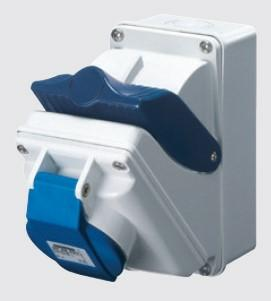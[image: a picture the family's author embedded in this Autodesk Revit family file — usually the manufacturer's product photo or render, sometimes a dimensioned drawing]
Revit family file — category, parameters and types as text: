
# Revit family: Building-ConnessioniIEC309-GEWISS-COMBIBLOC-PRESE-INTERBLOCCATE_IP44
name_source: partatom
category: Apparecchi elettrici
units: mm (PartAtom-declared; Revit-internal decimal feet)

## family parameters
Condiviso = No
Host = Superficie
Mantenere orientamento annotazione = Sì
Punto di calcolo locali = Sì
Quota connettore circolare = Usa diametro
Taglio con vuoti quando caricato = No
Tipo di parte = Normale

## types (18) — shared parameters
BLOCCO = B=C
Catalogo = BUILDING
Codice Electrocod = 2220
Con fondo = Si
FORMULA = 1000 mm  [stored 3.28084 ft]
Frequenza = 50/60 Hz
Glow wire test: = 850 °C (Parti attive) - 650 °C (Parti passive)
Grado di protezione = IP44
IDF = 30b8ffdf-9bd3-4092-bfeb-7357e213d0d1
IDT = 5f0ae1981d6d44abab9cf411e87918d1
Immagine tipo = COMBIBLOC44Fondo.jpg
L = 155 mm
N.poli = 1
POMELLO = bianco
PRESA = Giallo
Produttore = GEWISS S.p.A.
Prospetto di default = 1219 mm
Protezione = NO (SBF)
Resistenza agli urti = IK08
SEO = Presa interbloccata
STRUTTURA = RAL - 7035
STRUTTURA ALTA = blue
Scheda Tecnica = https://www.gewiss.com
Spostamento_S = 1500 mm
Temperatura di utilizzo = -25 +40 °C
Termopressione con biglia = 125 °C (Parti attive) - 80 °C (Parti passive)
Tipologia = Compatta
URL = https://www.gewiss.com
VETRO = Vetro
Versione file RFA = 21.4
Voltaggio = 0 V
W = 115 mm

## per-type parameters (varying)
| type | Colore: | Corrente nominale (A) | Descrizione | Modello | N. poli | Riferimento h | Tensione nominale |
| GW66405 - COMBIBLOC C.F.IP44 3P+T 16A 230V 9H | Blu | 16 | COMBIBLOC C.F.IP44 3P+T 16A 230V 9H | GW66405 | 3P+T | 9 | 200-250V |
| GW66403 - COMBIBLOC C.F.IP44 3P+N+T 16A 110V 4H | Giallo | 16 | COMBIBLOC C.F.IP44 3P+N+T 16A 110V 4H | GW66403 | 3P+N+T | 4 | 100-130V |
| GW66409 - COMBIBLOC C.F.IP44 3P+N+T 16A 400V 6H | Rosso | 16 | COMBIBLOC C.F.IP44 3P+N+T 16A 400V 6H | GW66409 | 3P+N+T | 6 | 380-415V |
| GW66402 - COMBIBLOC C.F.IP44 3P+T 16A 110V 4H | Giallo | 16 | COMBIBLOC C.F.IP44 3P+T 16A 110V 4H | GW66402 | 3P+T | 4 | 100-130V |
| GW66416 - COMBIBLOC C.F.IP44 3P+T 32A 230V 9H | Blu | 32 | COMBIBLOC C.F.IP44 3P+T 32A 230V 9H | GW66416 | 3P+T | 9 | 200-250V |
| GW66407 - COMBIBLOC C.F.IP44 2P+T 16A 400V 9H | Rosso | 16 | COMBIBLOC C.F.IP44 2P+T 16A 400V 9H | GW66407 | 2P+T | 9 | 380-415V |
| GW66417 - COMBIBLOC C.F.IP44 3P+N+T 32A 230V 9H | Blu | 32 | COMBIBLOC C.F.IP44 3P+N+T 32A 230V 9H | GW66417 | 3P+N+T | 9 | 200-250V |
| GW66404 - COMBIBLOC C.F.IP44 2P+T 16A 230V 6H | Blu | 16 | COMBIBLOC C.F.IP44 2P+T 16A 230V 6H | GW66404 | 2P+T | 6 | 200-250V |
| GW66412 - COMBIBLOC C.F.IP44 2P+T 32A 110V4H | Giallo | 32 | COMBIBLOC C.F.IP44 2P+T 32A 110V4H | GW66412 | 2P+T | 4 | 100-130V |
| GW66419 - COMBIBLOC C.F.IP44 3P+T 32A 400V 6H | Rosso | 32 | COMBIBLOC C.F.IP44 3P+T 32A 400V 6H | GW66419 | 3P+T | 6 | 380-415V |
| GW66413 - COMBIBLOC C.F.IP44 3P+T 32A 110V 4H | Giallo | 32 | COMBIBLOC C.F.IP44 3P+T 32A 110V 4H | GW66413 | 3P+T | 4 | 100-130V |
| GW66415 - COMBIBLOC C.F.IP44 2P+T 32A 230V 6H | Blu | 32 | COMBIBLOC C.F.IP44 2P+T 32A 230V 6H | GW66415 | 2P+T | 6 | 200-250V |
| GW66420 - COMBIBLOC C.F.IP44 3P+N+T 32A 400V 6H | Rosso | 32 | COMBIBLOC C.F.IP44 3P+N+T 32A 400V 6H | GW66420 | 3P+N+T | 6 | 380-415V |
| GW66414 - COMBIBLOC C.F.IP44 3P+N+T 32A 110V 4H | Giallo | 32 | COMBIBLOC C.F.IP44 3P+N+T 32A 110V 4H | GW66414 | 3P+N+T | 4 | 100-130V |
| GW66401 - COMBIBLOC C.F.IP44 2P+T 16A 110V 4H | Giallo | 16 | COMBIBLOC C.F.IP44 2P+T 16A 110V 4H | GW66401 | 2P+T | 4 | 100-130V |
| GW66408 - COMBIBLOC C.F.IP44 3P+T 16A 400V 6H | Rosso | 16 | COMBIBLOC C.F.IP44 3P+T 16A 400V 6H | GW66408 | 3P+T | 6 | 380-415V |
| GW66406 - COMBIBLOC C.F.IP44 3P+N+T 16A 230V 9H | Blu | 16 | COMBIBLOC C.F.IP44 3P+N+T 16A 230V 9H | GW66406 | 3P+N+T | 9 | 200-250V |
| GW66418 - COMBIBLOC C.F.IP44 2P+T 32A 400V 9H | Rosso | 32 | COMBIBLOC C.F.IP44 2P+T 32A 400V 9H | GW66418 | 2P+T | 9 | 380-415V |

note: [stored X ft] marks values corroborated as IEEE doubles in the binary element streams (Revit-internal decimal feet)

## geometry (parser evidence)
native form markers: Sweep x4
no freeform markers — native parametric forms only
